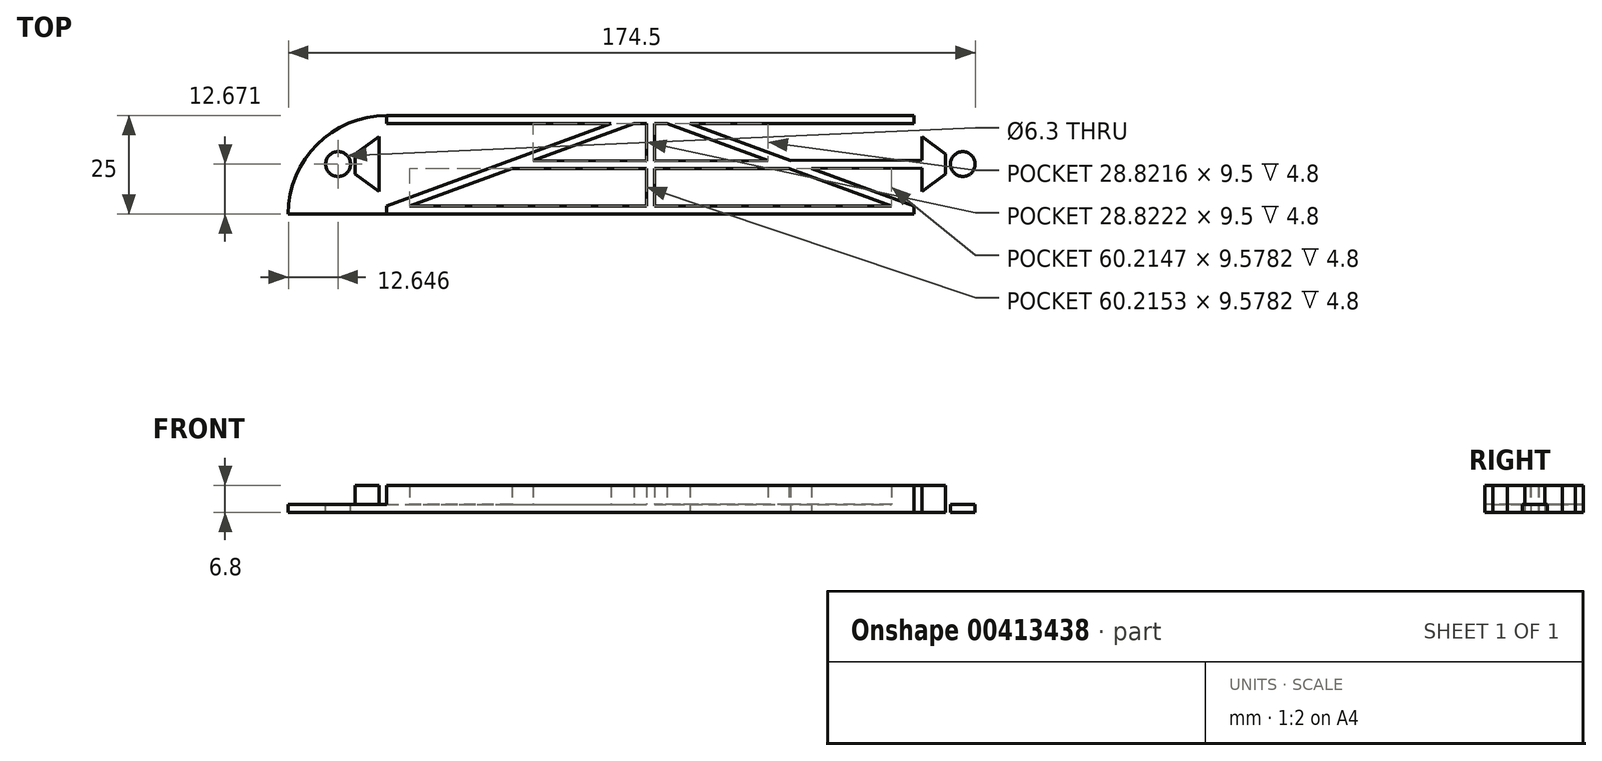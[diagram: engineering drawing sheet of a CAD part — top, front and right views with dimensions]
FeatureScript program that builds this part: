
annotation { "Feature Type Name" : "Feature", "Feature Type Description" : "" }
export const myFeature = defineFeature(function(context is Context, id is Id, definition is map)
    precondition{}
    {
        {
            var Q0;
            Q0=qCreatedBy(makeId("Top.planeOp"),FACE);
            var sketch = newSketch(context, id + "F0", { "sketchPlane" : qUnion([Q0])});
            skLineSegment(sketch, "E0.bottom", {"start": v(-4.14, 33.73) * mm, "end": v(129.86, 33.73) * mm});
            skLineSegment(sketch, "E0.top", {"start": v(-29.14, 8.73) * mm, "end": v(154.86, 8.73) * mm});
            skLineSegment(sketch, "E0.left", {"start": v(-29.14, 8.73) * mm, "end": v(-29.14, 8.73) * mm});
            skLineSegment(sketch, "E0.right", {"start": v(154.86, 8.73) * mm, "end": v(154.86, 8.73) * mm});
            skPoint(sketch, "E1.visualSharp", {"position": v(-29.14, 33.73) * mm});
            skArc(sketch, "E1.filletArc", {"start": v(-4.14, 33.73) * mm, "mid": v(-21.82, 26.41) * mm, "end": v(-29.14, 8.73) * mm});
            skPoint(sketch, "E2.visualSharp", {"position": v(154.86, 33.73) * mm});
            skArc(sketch, "E2.filletArc", {"start": v(154.86, 8.73) * mm, "mid": v(147.53, 26.41) * mm, "end": v(129.86, 33.73) * mm});
            skSolve(sketch);
        }
        {
            var Q0;
            Q0=makeQuery(id+"F0.imprint","IMPRINT",FACE,{"disambiguationData":[TD([[makeQuery(id+"F0.imprint","IMPRINT",EDGE,{"derivedFrom":sQuery(id+"F0.wireOp",EDGE,"E0.bottom")}),-1.0]])]});
            extrude(context, id + "F1", {"entities" : qUnion([Q0]), "depth" : 6.8 * mm});
        }
        {
            var Q0;
            Q0=makeQuery(id+"F1.opExtrude","CAP_FACE",FACE,{"disambiguationData":[OSD([sQuery(id+"F0.wireOp",EDGE,"E0.bottom"),sQuery(id+"F0.wireOp",EDGE,"E0.top"),sQuery(id+"F0.wireOp",EDGE,"E1.filletArc"),sQuery(id+"F0.wireOp",EDGE,"E2.filletArc")])],"isStart":false});
            shell(context, id + "F2", {"entities" : qUnion([Q0]), "thickness" : 2 * mm});
        }
        {
            var Q0;
            Q0=makeQuery(id+"F1.opExtrude","CAP_FACE",FACE,{"disambiguationData":[OSD([sQuery(id+"F0.wireOp",EDGE,"E0.bottom"),sQuery(id+"F0.wireOp",EDGE,"E0.top"),sQuery(id+"F0.wireOp",EDGE,"E1.filletArc"),sQuery(id+"F0.wireOp",EDGE,"E2.filletArc")])],"isStart":false});
            var sketch = newSketch(context, id + "F3", { "sketchPlane" : qUnion([Q0])});
            skLineSegment(sketch, "E3", {"start": v(-4.14, 10.73) * mm, "end": v(-4.14, 8.73) * mm});
            skLineSegment(sketch, "E4", {"start": v(129.86, 10.73) * mm, "end": v(129.86, 8.73) * mm});
            skLineSegment(sketch, "E5", {"start": v(129.86, 31.73) * mm, "end": v(129.86, 33.73) * mm});
            skLineSegment(sketch, "E6", {"start": v(-4.14, 31.73) * mm, "end": v(-4.14, 33.73) * mm});
            skSolve(sketch);
        }
        {
            var Q0;
            {var subQ3=sQuery(id+"F3.wireOp",EDGE,"E3");Q0=makeQuery(id+"F3.imprint","IMPRINT",FACE,{"disambiguationData":[TD([[makeQuery(id+"F3.imprint","IMPRINT",EDGE,{"derivedFrom":subQ3}),-1.0]])]});}
            var Q1;
            {var subQ3=sQuery(id+"F3.wireOp",EDGE,"E4");Q1=makeQuery(id+"F3.imprint","IMPRINT",FACE,{"disambiguationData":[TD([[makeQuery(id+"F3.imprint","IMPRINT",EDGE,{"derivedFrom":subQ3}),1.0]])]});}
            extrude(context, id + "F4", {"entities" : qUnion([Q0, Q1]), "operationType" : NewBodyOperationType.REMOVE, "oppositeDirection" : true, "depth" : 4.8 * mm});
        }
        {
            var Q0;
            {var subQ0=sQuery(id+"F0.wireOp",EDGE,"E2.filletArc");var subQ1=sQuery(id+"F0.wireOp",EDGE,"E0.top");var subQ2=sQuery(id+"F0.wireOp",EDGE,"E1.filletArc");Q0=makeQuery(id+"F4.boolean.opBoolean","MERGE",FACE,{"derivedFrom":[makeQuery(id+"F2.opShell","OFFSET_FACE",FACE,{"disambiguationData":[OSD([sQuery(id+"F0.wireOp",EDGE,"E0.bottom"),subQ1,subQ2,subQ0])]}),makeQuery(id+"F4.opExtrude","CAP_FACE",FACE,{"disambiguationData":[OSD([subQ1,subQ2,sQuery(id+"F3.wireOp",EDGE,"E3"),sQuery(id+"F3.wireOp",EDGE,"E6")])],"isStart":false}),makeQuery(id+"F4.opExtrude","CAP_FACE",FACE,{"disambiguationData":[OSD([subQ1,subQ0,sQuery(id+"F3.wireOp",EDGE,"E4"),sQuery(id+"F3.wireOp",EDGE,"E5")])],"isStart":false})]});}
            var sketch = newSketch(context, id + "F5", { "sketchPlane" : qUnion([Q0])});
            skLineSegment(sketch, "E7", {"start": v(62.86, 31.73) * mm, "end": v(54.86, 31.73) * mm});
            skLineSegment(sketch, "E8", {"start": v(-4.14, 10.73) * mm, "end": v(52.86, 31.73) * mm});
            skLineSegment(sketch, "E9", {"start": v(16.4, 16.17) * mm, "end": v(32.97, 22.28) * mm});
            skLineSegment(sketch, "E10", {"start": v(32.97, 22.28) * mm, "end": v(58.86, 31.81) * mm});
            skPoint(sketch, "E10.endSnap0", {"position": v(58.86, 31.73) * mm});
            skLineSegment(sketch, "E11", {"start": v(16.4, 16.17) * mm, "end": v(1.64, 10.73) * mm});
            skLineSegment(sketch, "E12", {"start": v(61.86, 31.73) * mm, "end": v(61.86, 10.73) * mm});
            skLineSegment(sketch, "E13.MirrorCS", {"start": v(63.86, 31.73) * mm, "end": v(63.86, 10.73) * mm});
            skLineSegment(sketch, "E14.MirrorCS", {"start": v(92.74, 22.28) * mm, "end": v(66.86, 31.81) * mm});
            skLineSegment(sketch, "E15.MirrorCS", {"start": v(109.32, 16.17) * mm, "end": v(92.74, 22.28) * mm});
            skLineSegment(sketch, "E16.MirrorCS", {"start": v(109.32, 16.17) * mm, "end": v(124.07, 10.73) * mm});
            skLineSegment(sketch, "E17.MirrorCS", {"start": v(129.86, 10.73) * mm, "end": v(72.86, 31.73) * mm});
            skPoint(sketch, "E18.endSnap0", {"position": v(61.86, 21.23) * mm});
            skLineSegment(sketch, "E19", {"start": v(-6.14, 21.39) * mm, "end": v(-6.14, 28.39) * mm});
            skLineSegment(sketch, "E20", {"start": v(-6.14, 21.39) * mm, "end": v(-6.14, 14.39) * mm});
            skLineSegment(sketch, "E21", {"start": v(-6.14, 21.39) * mm, "end": v(-6.14, 22.39) * mm});
            skLineSegment(sketch, "E22", {"start": v(-6.14, 21.39) * mm, "end": v(-6.14, 20.39) * mm});
            skLineSegment(sketch, "E23", {"start": v(-6.14, 20.39) * mm, "end": v(61.86, 20.23) * mm});
            skLineSegment(sketch, "E24", {"start": v(-6.14, 22.39) * mm, "end": v(61.86, 22.23) * mm});
            skLineSegment(sketch, "E25.MirrorCS", {"start": v(131.86, 22.39) * mm, "end": v(63.86, 22.23) * mm});
            skLineSegment(sketch, "E26.MirrorCS", {"start": v(131.86, 20.39) * mm, "end": v(63.86, 20.23) * mm});
            skCircle(sketch, "E27", {"center": v(-16.5, 21.4) * mm, "radius": 3.15 * mm});
            skCircle(sketch, "E28.MirrorC", {"center": v(142.2, 21.4) * mm, "radius": 3.15 * mm});
            skLineSegment(sketch, "E29", {"start": v(-12.14, 21.4) * mm, "end": v(-12.14, 23.9) * mm});
            skLineSegment(sketch, "E30", {"start": v(-12.14, 21.4) * mm, "end": v(-12.14, 18.9) * mm});
            skLineSegment(sketch, "E31", {"start": v(-12.14, 18.9) * mm, "end": v(-6.14, 14.39) * mm});
            skLineSegment(sketch, "E32", {"start": v(-12.14, 23.9) * mm, "end": v(-6.14, 28.39) * mm});
            skLineSegment(sketch, "E33", {"start": v(62.86, 31.73) * mm, "end": v(62.86, 10.73) * mm});
            skLineSegment(sketch, "E34.MirrorCS", {"start": v(131.86, 21.39) * mm, "end": v(131.86, 28.39) * mm});
            skLineSegment(sketch, "E35.MirrorCS", {"start": v(137.86, 23.9) * mm, "end": v(131.86, 28.39) * mm});
            skLineSegment(sketch, "E36.MirrorCS", {"start": v(131.86, 21.39) * mm, "end": v(131.86, 14.39) * mm});
            skLineSegment(sketch, "E37.MirrorCS", {"start": v(137.86, 18.9) * mm, "end": v(131.86, 14.39) * mm});
            skLineSegment(sketch, "E38.MirrorCS", {"start": v(137.86, 21.4) * mm, "end": v(137.86, 18.9) * mm});
            skLineSegment(sketch, "E39.MirrorCS", {"start": v(137.86, 21.4) * mm, "end": v(137.86, 23.9) * mm});
            skSolve(sketch);
        }
        {
            var Q0;
            Q0=makeQuery(id+"F5.imprint","IMPRINT",FACE,{"disambiguationData":[TD([[makeQuery(id+"F5.imprint","IMPRINT",EDGE,{"derivedFrom":sQuery(id+"F5.wireOp",EDGE,"E19")}),1.0]])]});
            var Q1;
            {var subQ4=sQuery(id+"F5.wireOp",EDGE,"E21");Q1=makeQuery(id+"F5.imprint","IMPRINT",FACE,{"disambiguationData":[TD([[makeQuery(id+"F5.imprint","IMPRINT",EDGE,{"derivedFrom":subQ4}),-1.0]])]});}
            var Q2;
            {var subQ5=sQuery(id+"F5.wireOp",EDGE,"E11");Q2=makeQuery(id+"F5.imprint","IMPRINT",FACE,{"disambiguationData":[TD([[makeQuery(id+"F5.imprint","IMPRINT",EDGE,{"derivedFrom":subQ5}),-1.0]])]});}
            var Q3;
            {var subQ5=sQuery(id+"F5.wireOp",EDGE,"E23");var subQ7=sQuery(id+"F5.wireOp",EDGE,"E8");var subQ8=makeQuery(id+"F5.imprint","INTERSECT",VERTEX,{"derivedFrom":[subQ7,subQ5]});Q3=makeQuery(id+"F5.imprint","IMPRINT",FACE,{"disambiguationData":[TD([[makeQuery(id+"F5.imprint","IMPRINT",EDGE,{"disambiguationData":[TD([[subQ8,-1.0]])],"derivedFrom":subQ7}),-1.0]])]});}
            var Q4;
            {var subQ3=sQuery(id+"F5.wireOp",EDGE,"E10");var subQ5=sQuery(id+"F5.wireOp",EDGE,"E7");var subQ6=makeQuery(id+"F5.imprint","INTERSECT",VERTEX,{"derivedFrom":[subQ5,subQ3]});Q4=makeQuery(id+"F5.imprint","IMPRINT",FACE,{"disambiguationData":[TD([[makeQuery(id+"F5.imprint","IMPRINT",EDGE,{"disambiguationData":[TD([[subQ6,1.0]])],"derivedFrom":subQ3}),1.0]])]});}
            var Q5;
            {var subQ3=sQuery(id+"F5.wireOp",EDGE,"E9");var subQ5=sQuery(id+"F5.wireOp",EDGE,"E10");var subQ6=makeQuery(id+"F5.imprint","INTERSECT",VERTEX,{"derivedFrom":[subQ3,subQ5]});Q5=makeQuery(id+"F5.imprint","IMPRINT",FACE,{"disambiguationData":[TD([[makeQuery(id+"F5.imprint","IMPRINT",EDGE,{"disambiguationData":[TD([[subQ6,1.0]])],"derivedFrom":subQ3}),-1.0]])]});}
            var Q6;
            {var subQ0=sQuery(id+"F5.wireOp",EDGE,"E12");var subQ5=sQuery(id+"F5.wireOp",EDGE,"E7");var subQ9=makeQuery(id+"F5.imprint","INTERSECT",VERTEX,{"derivedFrom":[subQ5,subQ0]});Q6=makeQuery(id+"F5.imprint","IMPRINT",FACE,{"disambiguationData":[TD([[makeQuery(id+"F5.imprint","IMPRINT",EDGE,{"disambiguationData":[TD([[subQ9,-1.0]])],"derivedFrom":subQ0}),1.0]])]});}
            var Q7;
            {var subQ0=sQuery(id+"F5.wireOp",EDGE,"E25.MirrorCS");var subQ1=sQuery(id+"F5.wireOp",EDGE,"E13.MirrorCS");var subQ2=makeQuery(id+"F5.imprint","INTERSECT",VERTEX,{"derivedFrom":[subQ1,subQ0]});Q7=makeQuery(id+"F5.imprint","IMPRINT",FACE,{"disambiguationData":[TD([[makeQuery(id+"F5.imprint","IMPRINT",EDGE,{"disambiguationData":[TD([[subQ2,-1.0]])],"derivedFrom":subQ1}),1.0]])]});}
            var Q8;
            {var subQ0=sQuery(id+"F5.wireOp",EDGE,"E25.MirrorCS");var subQ1=sQuery(id+"F5.wireOp",EDGE,"E14.MirrorCS");var subQ2=makeQuery(id+"F5.imprint","INTERSECT",VERTEX,{"derivedFrom":[subQ1,subQ0]});Q8=makeQuery(id+"F5.imprint","IMPRINT",FACE,{"disambiguationData":[TD([[makeQuery(id+"F5.imprint","IMPRINT",EDGE,{"disambiguationData":[TD([[subQ2,1.0]])],"derivedFrom":subQ0}),-1.0]])]});}
            var Q9;
            {var subQ5=sQuery(id+"F5.wireOp",EDGE,"E14.MirrorCS");var subQ7=sQuery(id+"F5.wireOp",EDGE,"E15.MirrorCS");var subQ8=makeQuery(id+"F5.imprint","INTERSECT",VERTEX,{"derivedFrom":[subQ5,subQ7]});Q9=makeQuery(id+"F5.imprint","IMPRINT",FACE,{"disambiguationData":[TD([[makeQuery(id+"F5.imprint","IMPRINT",EDGE,{"disambiguationData":[TD([[subQ8,-1.0]])],"derivedFrom":subQ5}),-1.0]])]});}
            var Q10;
            {var subQ5=sQuery(id+"F5.wireOp",EDGE,"E16.MirrorCS");Q10=makeQuery(id+"F5.imprint","IMPRINT",FACE,{"disambiguationData":[TD([[makeQuery(id+"F5.imprint","IMPRINT",EDGE,{"derivedFrom":subQ5}),1.0]])]});}
            var Q11;
            {var subQ5=sQuery(id+"F5.wireOp",EDGE,"E26.MirrorCS");var subQ6=sQuery(id+"F5.wireOp",EDGE,"E17.MirrorCS");var subQ7=makeQuery(id+"F5.imprint","INTERSECT",VERTEX,{"derivedFrom":[subQ6,subQ5]});Q11=makeQuery(id+"F5.imprint","IMPRINT",FACE,{"disambiguationData":[TD([[makeQuery(id+"F5.imprint","IMPRINT",EDGE,{"disambiguationData":[TD([[subQ7,-1.0]])],"derivedFrom":subQ6}),-1.0]])]});}
            var Q12;
            {var subQ2=sQuery(id+"F5.wireOp",EDGE,"f90c1f64-840c-4de0-9133-70b325553d000.MirrorCS");Q12=makeQuery(id+"F5.imprint","IMPRINT",FACE,{"disambiguationData":[TD([[makeQuery(id+"F5.imprint","IMPRINT",EDGE,{"derivedFrom":subQ2}),-1.0]])]});}
            var Q13;
            {var subQ4=sQuery(id+"F5.wireOp",EDGE,"E35.MirrorCS");Q13=makeQuery(id+"F5.imprint","IMPRINT",FACE,{"disambiguationData":[TD([[makeQuery(id+"F5.imprint","IMPRINT",EDGE,{"derivedFrom":subQ4}),1.0]])]});}
            var Q14;
            {var subQ0=sQuery(id+"F5.wireOp",EDGE,"E33");Q14=makeQuery(id+"F5.imprint","IMPRINT",FACE,{"disambiguationData":[TD([[makeQuery(id+"F5.imprint","IMPRINT",EDGE,{"derivedFrom":subQ0}),1.0]])]});}
            extrude(context, id + "F6", {"entities" : qUnion([Q0, Q1, Q2, Q3, Q4, Q5, Q6, Q7, Q8, Q9, Q10, Q11, Q12, Q13, Q14]), "operationType" : NewBodyOperationType.ADD, "depth" : 4.8 * mm});
        }
        {
            var Q0;
            Q0=makeQuery(id+"F5.imprint","IMPRINT",FACE,{"disambiguationData":[TD([[makeQuery(id+"F5.imprint","IMPRINT",EDGE,{"derivedFrom":sQuery(id+"F5.wireOp",EDGE,"E27")}),1.0]])]});
            var Q1;
            Q1=makeQuery(id+"F5.imprint","IMPRINT",FACE,{"disambiguationData":[TD([[makeQuery(id+"F5.imprint","IMPRINT",EDGE,{"derivedFrom":sQuery(id+"F5.wireOp",EDGE,"E28.MirrorC")}),-1.0]])]});
            extrude(context, id + "F7", {"entities" : qUnion([Q0, Q1]), "operationType" : NewBodyOperationType.REMOVE, "oppositeDirection" : true, "depth" : 2 * mm});
        }
    });
